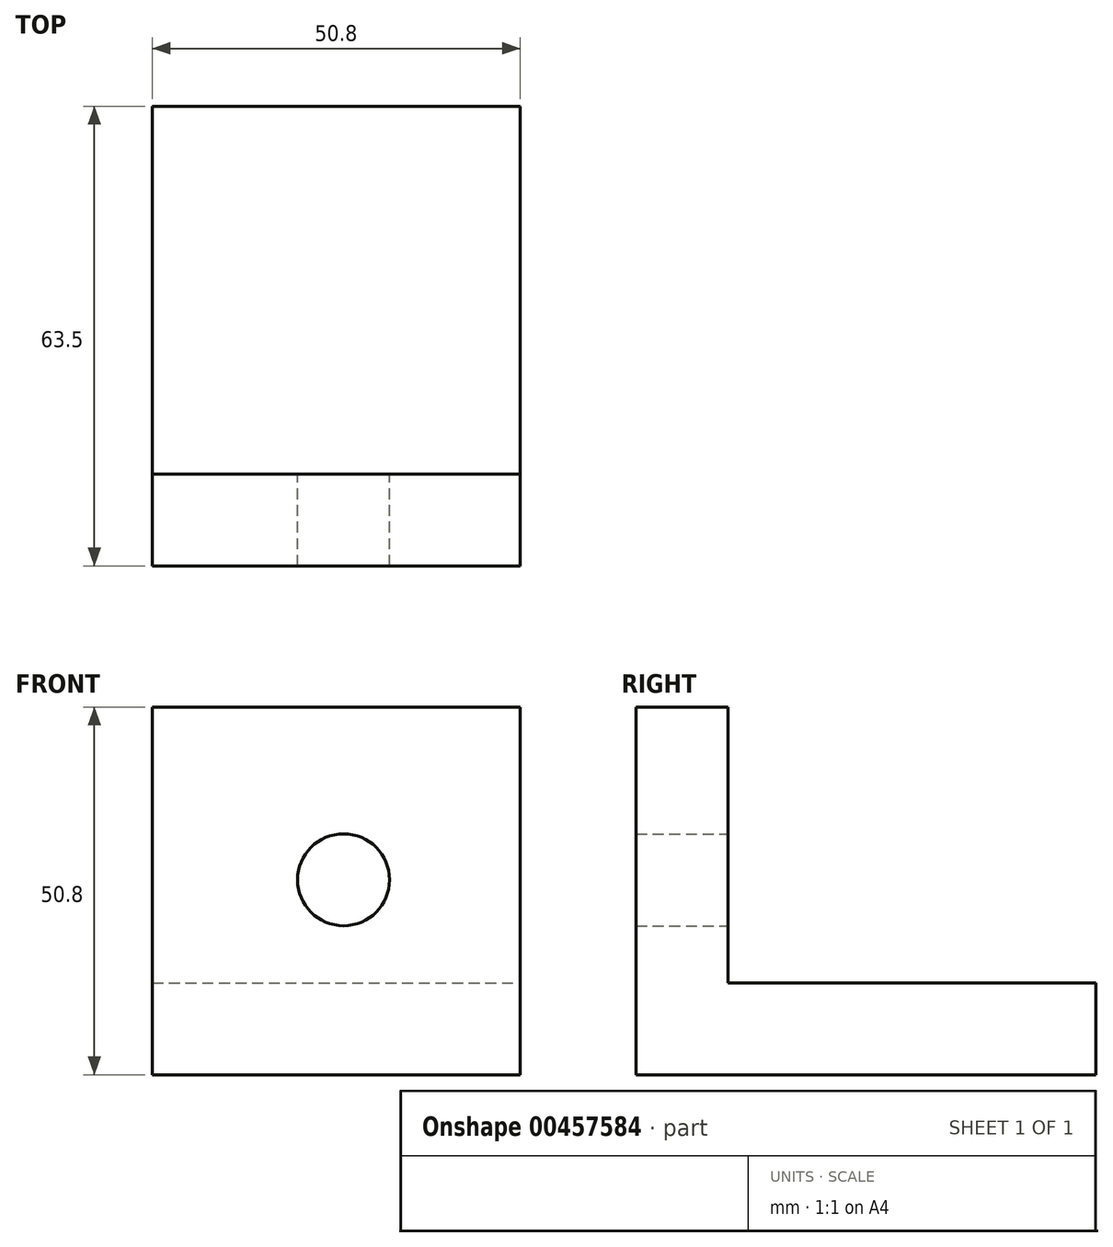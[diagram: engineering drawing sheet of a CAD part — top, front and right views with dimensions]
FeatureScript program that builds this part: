
annotation { "Feature Type Name" : "Feature", "Feature Type Description" : "" }
export const myFeature = defineFeature(function(context is Context, id is Id, definition is map)
    precondition{}
    {
        {
            var Q0;
            Q0=qCreatedBy(makeId("Front.planeOp"),FACE);
            var sketch = newSketch(context, id + "F0", { "sketchPlane" : qUnion([Q0])});
            skLineSegment(sketch, "E0.bottom", {"start": v(0, 0) * mm, "end": v(50.8, 0) * mm});
            skLineSegment(sketch, "E0.top", {"start": v(0, 50.8) * mm, "end": v(50.8, 50.8) * mm});
            skLineSegment(sketch, "E0.left", {"start": v(0, 0) * mm, "end": v(0, 50.8) * mm});
            skLineSegment(sketch, "E0.right", {"start": v(50.8, 0) * mm, "end": v(50.8, 50.8) * mm});
            skCircle(sketch, "E1", {"center": v(26.41, 26.93) * mm, "radius": 6.35 * mm});
            skSolve(sketch);
        }
        {
            var Q0;
            Q0=qCreatedBy(makeId("Top.planeOp"),FACE);
            var sketch = newSketch(context, id + "F1", { "sketchPlane" : qUnion([Q0])});
            skLineSegment(sketch, "E2.bottom", {"start": v(0, 0) * mm, "end": v(50.8, 0) * mm});
            skLineSegment(sketch, "E2.top", {"start": v(0, 50.8) * mm, "end": v(50.8, 50.8) * mm});
            skLineSegment(sketch, "E2.left", {"start": v(0, 0) * mm, "end": v(0, 50.8) * mm});
            skLineSegment(sketch, "E2.right", {"start": v(50.8, 0) * mm, "end": v(50.8, 50.8) * mm});
            skSolve(sketch);
        }
        {
            var Q0;
            Q0=makeQuery(id+"F0.imprint","IMPRINT",FACE,{"disambiguationData":[TD([[makeQuery(id+"F0.imprint","IMPRINT",EDGE,{"derivedFrom":sQuery(id+"F0.wireOp",EDGE,"E0.bottom")}),1.0]])]});
            extrude(context, id + "F2", {"entities" : qUnion([Q0]), "depth" : 12.7 * mm});
        }
        {
            var Q0;
            Q0=makeQuery(id+"F1.imprint","IMPRINT",FACE,{"disambiguationData":[TD([[makeQuery(id+"F1.imprint","IMPRINT",EDGE,{"derivedFrom":sQuery(id+"F1.wireOp",EDGE,"E2.bottom")}),1.0]])]});
            extrude(context, id + "F3", {"entities" : qUnion([Q0]), "operationType" : NewBodyOperationType.ADD, "depth" : 12.7 * mm});
        }
    });
